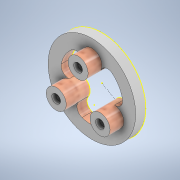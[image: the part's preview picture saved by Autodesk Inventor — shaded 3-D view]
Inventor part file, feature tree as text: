
AUTODESK INVENTOR PART (.ipt)
format: ipt  version: 2021 (Build 250183000, 183)  size: 371,712 bytes
history: native  units: mm
features: projected_geometry x6, sketch x5, extrude x4, reference x3, other x3, fillet x1
ambient origin geometry x8: Origin, YZ Plane, XZ Plane, XY Plane, X Axis, Y Axis, Z Axis, Center Point
bodies: Body1 (feature_tree)
feature tree (22):
  extrude  "Extrusion2"  Depth=4.0mm TaperAngle=0.0deg
  extrude  "Extrusion3"  Depth=3.0mm
  fillet  "Fillet1"  Radius=3.0mm
  sketch  "Boceto4"  dims[d25=3.0mm d26=1.5mm d27=0.0mm]
  extrude  "Extrusion5"  Depth=1.5mm TaperAngle=0.0deg
  extrude  "Extrusion6"  Depth=3.0mm
  sketch  "Sketch1"  dims[d11=30.0mm d12=5.0mm d13=8.0mm d14=5.0mm d15=1.5mm d16=360.0deg d18=25.0mm d19=4.0mm d20=0.0mm]
  reference  "Reference1"
  reference  "Reference2"
  reference  "Reference3"
  sketch  "Sketch3"  dims[d22=3.0mm d23=3.0mm d24=3.0mm]
  projected_geometry  "Projected Loop1"
  projected_geometry  "Contorno proyectado2"
  sketch  "Sketch5"  dims[d28=2.0mm d29=3.0mm]
  projected_geometry  "Projected Loop3"
  sketch  "Sketch6"  dims[d32=4.0mm d33=0.0mm d34=3.5mm d35=3.5mm d36=3.5mm d37=1.5mm d38=0.0mm d10=0.5mm]
  projected_geometry  "Projected Loop4"
  projected_geometry  "Projected Loop5"
  projected_geometry  "Projected Loop6"
  other  "Z:\softHandProsthesis.iam"
  other  "softHandProsthesis.iam"
  other  "palm_socket_connector:1"
